# Revit family: 03-30-005 DN25-50
name_source: partatom
category: Pipe Accessories
units: mm (PartAtom-declared; Revit-internal decimal feet)

## family parameters
Always vertical = Yes
Cut with Voids When Loaded = No
Part Type = Valve - Breaks Into
Round Connector Dimension = Use Diameter
Shared = No
Work Plane-Based = No

## types (5) — shared parameters
1 = 1 mm  [stored 0.00328084 ft]
10 = 10 mm  [stored 0.0328084 ft]
15 = 15 mm  [stored 0.0492126 ft]
6 = 6 mm  [stored 0.019685 ft]
Bonnet_R = 13 mm  [stored 0.0426509 ft]
DN020_PN16 = 03-025-30-0046499
DN025_PN16 = 03-032-30-0046499
 03-032-30-0046499
03-032-30-0046499
03-032-30-0046499
03-032-30-0046499
DN032_PN16 = 03-040-30-0046499
DN040_PN16 = 03-050-30-00
DN050_PN16 = 03-063-30-00
Description_ = AVK SERVICE CONNECTION VALVE, DI, PN16
F = 6 mm  [stored 0.019685 ft]
F1 = 9 mm  [stored 0.0295276 ft]
F11 = 11 mm  [stored 0.0360892 ft]
F12 = 8 mm  [stored 0.0262467 ft]
F2 = 35 mm  [stored 0.114829 ft]
F3 = 13 mm  [stored 0.0426509 ft]
F4 = 16 mm  [stored 0.0524934 ft]
F5 = 30 mm  [stored 0.0984252 ft]
Search_table = 03-30-005 DN25-50
T = 5 mm  [stored 0.0164042 ft]
URL_product_pages = https://www.avkvalves.com
zero-valued in all types: 0, Default Elevation

## per-type parameters (varying)
- DN020_PN16: Body_H=56 mm; Body_L=31 mm  [stored 0.101706 ft]; Body_L1=34 mm; Body_L2=40 mm  [stored 0.131234 ft]; Body_L3=24 mm  [stored 0.0787402 ft]; Body_Rib_L=7 mm  [stored 0.0229659 ft]; Body_T=20 mm  [stored 0.0656168 ft]; Body_W=26 mm; Body_rib1=32 mm  [stored 0.104987 ft]; Bore=10 mm  [stored 0.0328084 ft]; D1=16 mm  [stored 0.0524934 ft]; D2=18 mm  [stored 0.0590551 ft]; DN=20 mm  [stored 0.0656168 ft]; Dd=14 mm  [stored 0.0459318 ft]; Dd1=21 mm  [stored 0.0688976 ft]; F6=31 mm  [stored 0.101706 ft]; H=163 mm; H3=187 mm; H3-H=24 mm  [stored 0.0787402 ft]; L=82 mm; L1=110 mm; L2=41 mm  [stored 0.134514 ft]; L3=45 mm  [stored 0.147638 ft]; O1=27 mm  [stored 0.0885827 ft]; O2=16 mm  [stored 0.0524934 ft]; Od11=19 mm; Rib_L=25 mm  [stored 0.082021 ft]; Thickness=7 mm  [stored 0.0229659 ft]; W=36 mm  [stored 0.11811 ft]; bonnet_L=51 mm; bonnet_W=36 mm  [stored 0.11811 ft]
- DN025_PN16: Body_H=56 mm; Body_L=31 mm  [stored 0.101706 ft]; Body_L1=34 mm; Body_L2=40 mm  [stored 0.131234 ft]; Body_L3=24 mm  [stored 0.0787402 ft]; Body_Rib_L=8 mm  [stored 0.0262467 ft]; Body_T=20 mm  [stored 0.0656168 ft]; Body_W=26 mm; Body_rib1=32 mm  [stored 0.104987 ft]; Bore=13 mm  [stored 0.0426509 ft]; D1=18 mm  [stored 0.0590551 ft]; D2=21 mm  [stored 0.0688976 ft]; DN=25 mm  [stored 0.082021 ft]; Dd=16 mm  [stored 0.0524934 ft]; Dd1=25 mm  [stored 0.082021 ft]; F6=31 mm  [stored 0.101706 ft]; H=163 mm; H3=192 mm; H3-H=29 mm  [stored 0.0951444 ft]; L=93 mm; L1=110 mm; L2=46 mm; L3=51 mm; O1=27 mm  [stored 0.0885827 ft]; O2=16 mm  [stored 0.0524934 ft]; Od11=23 mm  [stored 0.0754593 ft]; Rib_L=25 mm  [stored 0.082021 ft]; Thickness=7 mm  [stored 0.0229659 ft]; W=36 mm  [stored 0.11811 ft]; bonnet_L=51 mm; bonnet_W=36 mm  [stored 0.11811 ft]
- DN032_PN16: Body_H=69 mm; Body_L=31 mm  [stored 0.101706 ft]; Body_L1=34 mm; Body_L2=40 mm  [stored 0.131234 ft]; Body_L3=24 mm  [stored 0.0787402 ft]; Body_Rib_L=11 mm  [stored 0.0360892 ft]; Body_T=20 mm  [stored 0.0656168 ft]; Body_W=26 mm; Body_rib1=32 mm  [stored 0.104987 ft]; Bore=16 mm  [stored 0.0524934 ft]; D1=25 mm  [stored 0.082021 ft]; D2=28 mm; DN=32 mm  [stored 0.104987 ft]; Dd=22 mm; Dd1=29 mm  [stored 0.0951444 ft]; F6=31 mm  [stored 0.101706 ft]; H=176 mm; H3=208 mm; H3-H=32 mm  [stored 0.104987 ft]; L=103 mm; L1=120 mm; L2=51 mm; L3=56 mm; O1=30 mm  [stored 0.0984252 ft]; O2=21 mm  [stored 0.0688976 ft]; Od11=26 mm; Rib_L=25 mm  [stored 0.082021 ft]; Thickness=7 mm  [stored 0.0229659 ft]; W=36 mm  [stored 0.11811 ft]; bonnet_L=51 mm; bonnet_W=36 mm  [stored 0.11811 ft]
- DN040_PN16: Body_H=99 mm; Body_L=44 mm; Body_L1=48 mm; Body_L2=57 mm; Body_L3=35 mm  [stored 0.114829 ft]; Body_Rib_L=13 mm  [stored 0.0426509 ft]; Body_T=29 mm  [stored 0.0951444 ft]; Body_W=38 mm  [stored 0.124672 ft]; Body_rib1=46 mm; Bore=20 mm  [stored 0.0656168 ft]; D1=30 mm  [stored 0.0984252 ft]; D2=34 mm; DN=40 mm  [stored 0.131234 ft]; Dd=26 mm; Dd1=31 mm  [stored 0.101706 ft]; F6=44 mm; H=224 mm; H3=262 mm; H3-H=38 mm  [stored 0.124672 ft]; L=128 mm; L1=151 mm; L2=64 mm; L3=70 mm; O1=36 mm  [stored 0.11811 ft]; O2=26 mm; Od11=30 mm  [stored 0.0984252 ft]; Rib_L=36 mm  [stored 0.11811 ft]; Thickness=10 mm  [stored 0.0328084 ft]; W=45 mm  [stored 0.147638 ft]; bonnet_L=63 mm; bonnet_W=45 mm  [stored 0.147638 ft]
- DN050_PN16: Body_H=110 mm; Body_L=44 mm; Body_L1=48 mm; Body_L2=57 mm; Body_L3=35 mm  [stored 0.114829 ft]; Body_Rib_L=17 mm; Body_T=30 mm  [stored 0.0984252 ft]; Body_W=38 mm  [stored 0.124672 ft]; Body_rib1=46 mm; Bore=25 mm  [stored 0.082021 ft]; D1=39 mm; D2=44 mm; DN=50 mm; Dd=34 mm; Dd1=35 mm  [stored 0.114829 ft]; F6=44 mm; H=234 mm; H3=282 mm; H3-H=48 mm; L=153 mm; L1=176 mm; L2=77 mm; L3=84 mm; O1=43 mm  [stored 0.141076 ft]; O2=32 mm  [stored 0.104987 ft]; Od11=38 mm  [stored 0.124672 ft]; Rib_L=36 mm  [stored 0.11811 ft]; Thickness=11 mm  [stored 0.0360892 ft]; W=45 mm  [stored 0.147638 ft]; bonnet_L=63 mm; bonnet_W=45 mm  [stored 0.147638 ft]

note: [stored X ft] marks values corroborated as IEEE doubles in the binary element streams (Revit-internal decimal feet)

## geometry (parser evidence)
native form markers: Sweep x5
no freeform markers — native parametric forms only
